# Revit family: Урна 120-151 Арт 7340
name_source: partatom
category: Антураж
revit_build: Autodesk Revit 2018 (Build: 20180423_1000(x64)
units: mm (PartAtom-declared; Revit-internal decimal feet)

## family parameters
Всегда вертикально = Да
Источник визуального образа = Геометрия семейства
На основе рабочей плоскости = Нет
Общий = Нет
При загрузке вырезать с полостями = Нет
Точка расчета площади = Нет

## types (2) — shared parameters
URL = https://hobbyka.ru
Артикул товара = Арт. 7340
Группа модели = Уличные урны
Изготовитель = ООО «Хоббика»
Изображение типоразмера = Урна 120-151 Арт 7340.jpg
Материал изделия = Сталь
Цвет каркаса = Сталь
Цвет урны = Урнв

## per-type parameters (varying)
| type | Версия 20 л | Версия 30 л | Внут.диаметр | Высота | Диаметр урны | Длина | Крепление | Описание | Ширина |
| Версия 20 л | Да | Нет | 256 мм | 500 мм | 260 мм | 320 мм | 190 мм | Урна 120/151. Версия 20 л | 320 мм |
| Версия 30 л | Нет | Да | 296 мм | 580 мм | 300 мм | 360 мм | 220 мм | Урна 120/151. Версия 30 л | 380 мм |
